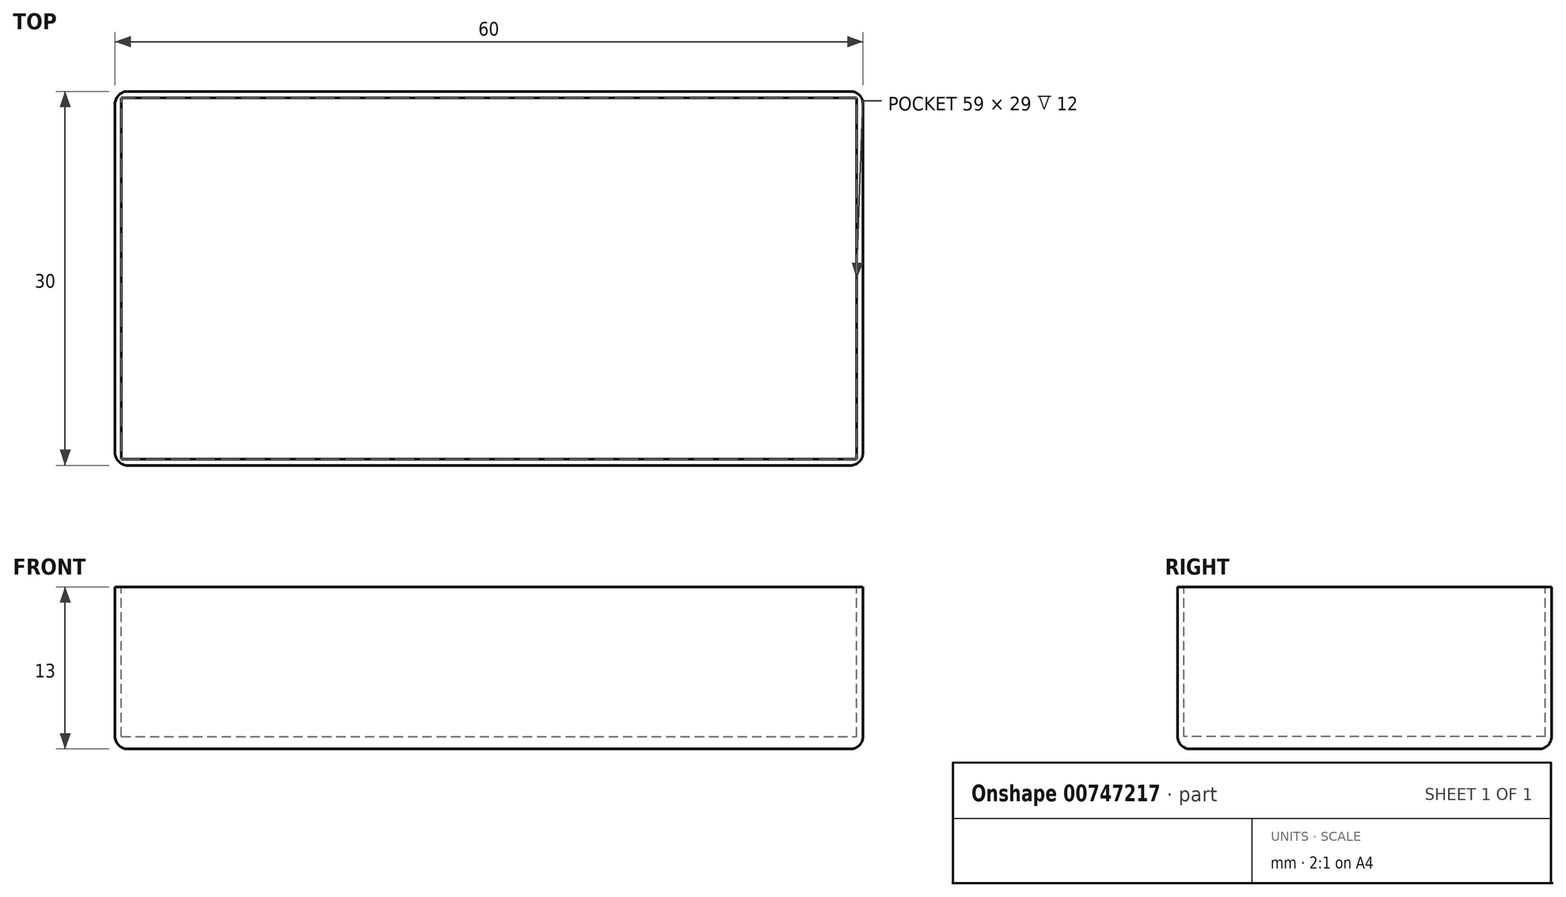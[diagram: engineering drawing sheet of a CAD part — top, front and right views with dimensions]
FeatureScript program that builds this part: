
annotation { "Feature Type Name" : "Feature", "Feature Type Description" : "" }
export const myFeature = defineFeature(function(context is Context, id is Id, definition is map)
    precondition{}
    {
        {
            var Q0;
            Q0=qCreatedBy(makeId("Top.planeOp"),FACE);
            var sketch = newSketch(context, id + "F0", { "sketchPlane" : qUnion([Q0])});
            skLineSegment(sketch, "E0.bottom", {"start": v(30, -15) * mm, "end": v(-30, -15) * mm});
            skLineSegment(sketch, "E0.top", {"start": v(30, 15) * mm, "end": v(-30, 15) * mm});
            skLineSegment(sketch, "E0.left", {"start": v(30, -15) * mm, "end": v(30, 15) * mm});
            skLineSegment(sketch, "E0.right", {"start": v(-30, -15) * mm, "end": v(-30, 15) * mm});
            skPoint(sketch, "E0.middle", {"position": v(0, 0) * mm});
            skLineSegment(sketch, "E1.bottom", {"start": v(-29.5, 14.5) * mm, "end": v(29.5, 14.5) * mm});
            skLineSegment(sketch, "E1.top", {"start": v(-29.5, -14.5) * mm, "end": v(29.5, -14.5) * mm});
            skLineSegment(sketch, "E1.left", {"start": v(-29.5, 14.5) * mm, "end": v(-29.5, -14.5) * mm});
            skLineSegment(sketch, "E1.right", {"start": v(29.5, 14.5) * mm, "end": v(29.5, -14.5) * mm});
            skSolve(sketch);
        }
        {
            var Q0;
            Q0=makeQuery(id+"F0.imprint","IMPRINT",FACE,{"disambiguationData":[TD([[makeQuery(id+"F0.imprint","IMPRINT",EDGE,{"derivedFrom":sQuery(id+"F0.wireOp",EDGE,"E0.bottom")}),-1.0]])]});
            var Q1;
            Q1=makeQuery(id+"F0.imprint","IMPRINT",FACE,{"disambiguationData":[TD([[makeQuery(id+"F0.imprint","IMPRINT",EDGE,{"derivedFrom":sQuery(id+"F0.wireOp",EDGE,"E1.bottom")}),-1.0]])]});
            extrude(context, id + "F1", {"entities" : qUnion([Q0, Q1]), "oppositeDirection" : true, "depth" : 13 * mm, "offsetDistance" : 25 * mm});
        }
        {
            var Q0;
            Q0=makeQuery(id+"F0.imprint","IMPRINT",FACE,{"disambiguationData":[TD([[makeQuery(id+"F0.imprint","IMPRINT",EDGE,{"derivedFrom":sQuery(id+"F0.wireOp",EDGE,"E1.bottom")}),-1.0]])]});
            extrude(context, id + "F2", {"entities" : qUnion([Q0]), "operationType" : NewBodyOperationType.REMOVE, "oppositeDirection" : true, "depth" : 12 * mm, "offsetDistance" : 25 * mm});
        }
        {
            var Q0;
            Q0=makeQuery(id+"F1.opExtrude","CAP_EDGE",EDGE,{"disambiguationData":[OSD([sQuery(id+"F0.wireOp",EDGE,"E0.right")])],"isStart":false});
            var Q1;
            Q1=makeQuery(id+"F1.opExtrude","SWEPT_EDGE",EDGE,{"disambiguationData":[OSD([sQuery(id+"F0.wireOp",EDGE,"E0.top"),sQuery(id+"F0.wireOp",EDGE,"E0.right")])]});
            var Q2;
            Q2=makeQuery(id+"F1.opExtrude","CAP_EDGE",EDGE,{"disambiguationData":[OSD([sQuery(id+"F0.wireOp",EDGE,"E0.top")])],"isStart":false});
            var Q3;
            Q3=makeQuery(id+"F1.opExtrude","SWEPT_EDGE",EDGE,{"disambiguationData":[OSD([sQuery(id+"F0.wireOp",EDGE,"E0.top"),sQuery(id+"F0.wireOp",EDGE,"E0.left")])]});
            var Q4;
            Q4=makeQuery(id+"F1.opExtrude","CAP_EDGE",EDGE,{"disambiguationData":[OSD([sQuery(id+"F0.wireOp",EDGE,"E0.left")])],"isStart":false});
            var Q5;
            Q5=makeQuery(id+"F1.opExtrude","CAP_EDGE",EDGE,{"disambiguationData":[OSD([sQuery(id+"F0.wireOp",EDGE,"E0.bottom")])],"isStart":false});
            var Q6;
            Q6=makeQuery(id+"F1.opExtrude","SWEPT_EDGE",EDGE,{"disambiguationData":[OSD([sQuery(id+"F0.wireOp",EDGE,"E0.bottom"),sQuery(id+"F0.wireOp",EDGE,"E0.left")])]});
            var Q7;
            Q7=makeQuery(id+"F1.opExtrude","SWEPT_EDGE",EDGE,{"disambiguationData":[OSD([sQuery(id+"F0.wireOp",EDGE,"E0.bottom"),sQuery(id+"F0.wireOp",EDGE,"E0.right")])]});
            fillet(context, id + "F3", {"entities" : qUnion([Q0, Q1, Q2, Q3, Q4, Q5, Q6, Q7]), "radius" : 1 * mm, "tangentPropagation" : true, "allowEdgeOverflow" : false});
        }
    });
